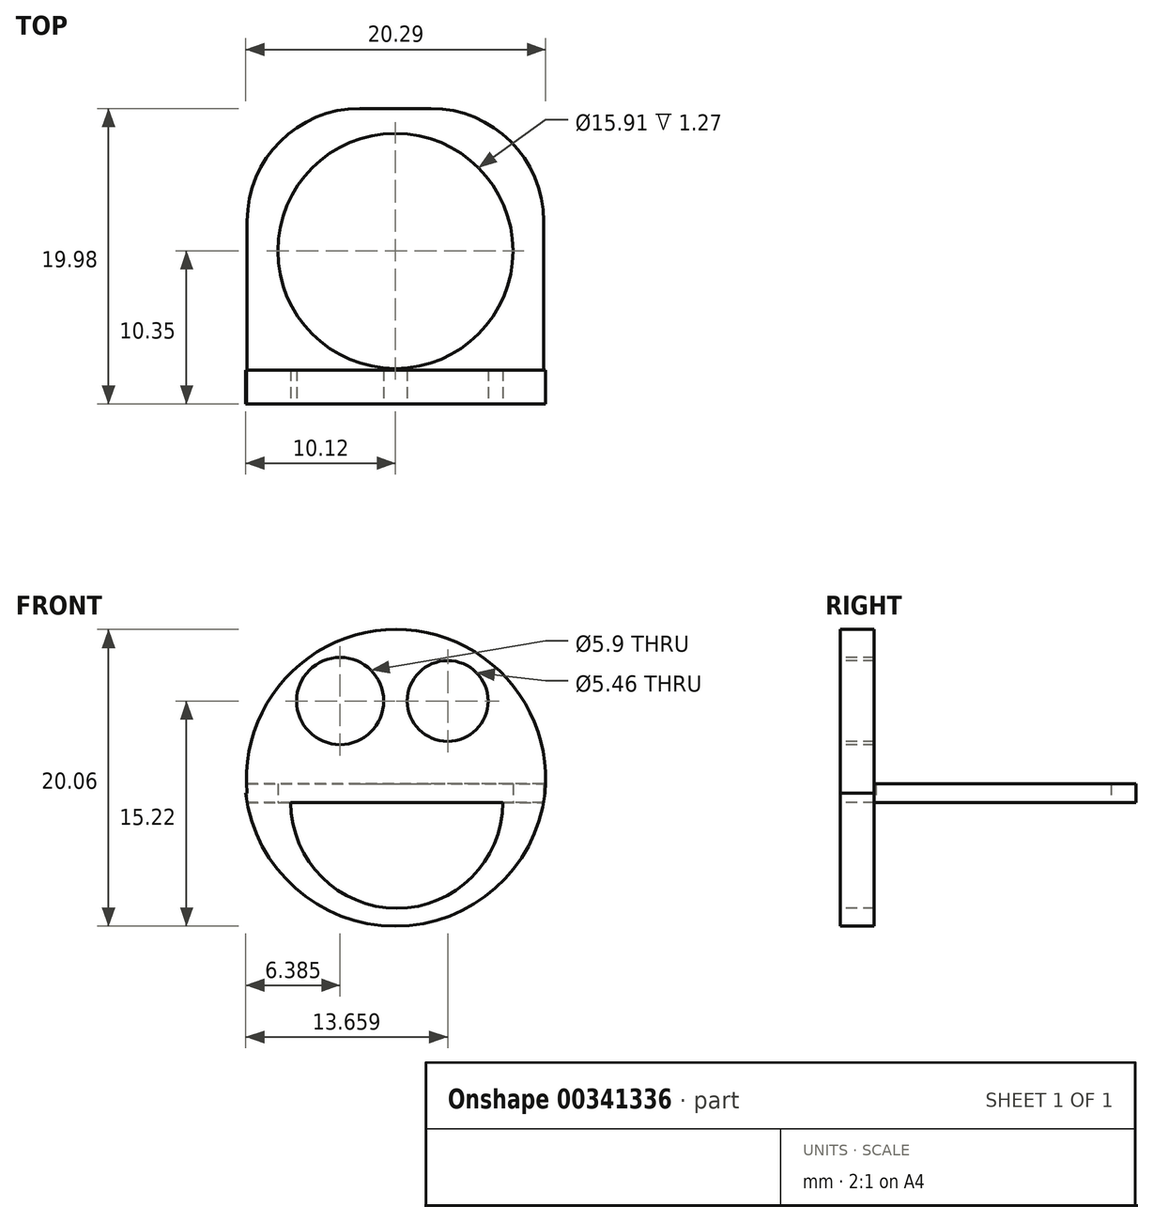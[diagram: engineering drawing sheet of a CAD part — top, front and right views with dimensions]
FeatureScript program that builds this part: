
annotation { "Feature Type Name" : "Feature", "Feature Type Description" : "" }
export const myFeature = defineFeature(function(context is Context, id is Id, definition is map)
    precondition{}
    {
        {
            var Q0;
            Q0=qCreatedBy(makeId("Top.planeOp"),FACE);
            var sketch = newSketch(context, id + "F0", { "sketchPlane" : qUnion([Q0])});
            skCircle(sketch, "E0", {"center": v(0, 0) * mm, "radius": 7.95 * mm});
            skLineSegment(sketch, "E1.bottom", {"start": v(-10.03, 9.63) * mm, "end": v(10.03, 9.63) * mm});
            skLineSegment(sketch, "E1.top", {"start": v(-10.03, -8.06) * mm, "end": v(10.03, -8.06) * mm});
            skLineSegment(sketch, "E1.left", {"start": v(-10.03, 9.63) * mm, "end": v(-10.03, -8.06) * mm});
            skLineSegment(sketch, "E1.right", {"start": v(10.03, 9.63) * mm, "end": v(10.03, -8.06) * mm});
            skSolve(sketch);
        }
        {
            var Q0;
            Q0 = qSketchRegion(id + "F0", true);
            extrude(context, id + "F1", {"entities" : qUnion([Q0]), "depth" : 1.27 * mm});
        }
        {
            var Q0;
            Q0=makeQuery(id+"F1.opExtrude","SWEPT_EDGE",EDGE,{"disambiguationData":[OSD([sQuery(id+"F0.wireOp",EDGE,"E1.bottom"),sQuery(id+"F0.wireOp",EDGE,"E1.left")])]});
            var Q1;
            Q1=makeQuery(id+"F1.opExtrude","SWEPT_EDGE",EDGE,{"disambiguationData":[OSD([sQuery(id+"F0.wireOp",EDGE,"E1.bottom"),sQuery(id+"F0.wireOp",EDGE,"E1.right")])]});
            fillet(context, id + "F2", {"entities" : qUnion([Q0, Q1]), "radius" : 7.62 * mm, "tangentPropagation" : true, "allowEdgeOverflow" : false});
        }
        {
            var Q0;
            Q0=makeQuery(id+"F1.opExtrude","SWEPT_FACE",FACE,{"disambiguationData":[OSD([sQuery(id+"F0.wireOp",EDGE,"E1.top")])]});
            var sketch = newSketch(context, id + "F3", { "sketchPlane" : qUnion([Q0])});
            skArc(sketch, "E2", {"start": v(-10.12, 0.64) * mm, "mid": v(0, -8.34) * mm, "end": v(10.12, 0.63) * mm});
            skPoint(sketch, "E2.centerSnap0", {"position": v(0, 1.27) * mm});
            skPoint(sketch, "E3.startSnap0", {"position": v(10.03, 0.64) * mm});
            skPoint(sketch, "E3.endSnap0", {"position": v(-10.03, 0.64) * mm});
            skLineSegment(sketch, "E4", {"start": v(-10.12, 0.64) * mm, "end": v(10.12, 0.64) * mm});
            skArc(sketch, "E5", {"start": v(10.12, 0.64) * mm, "mid": v(0.05, 11.72) * mm, "end": v(-10.03, 0.64) * mm});
            skSolve(sketch);
        }
        {
            var Q0;
            Q0 = qSketchRegion(id + "F3", true);
            extrude(context, id + "F4", {"entities" : qUnion([Q0]), "operationType" : NewBodyOperationType.ADD, "depth" : 2.3 * mm});
        }
        {
            var Q0;
            Q0=makeQuery(id+"F4.opExtrude","CAP_FACE",FACE,{"disambiguationData":[OSD([sQuery(id+"F3.wireOp",EDGE,"E2"),sQuery(id+"F3.wireOp",EDGE,"E4"),sQuery(id+"F3.wireOp",EDGE,"E5")])],"isStart":false});
            var sketch = newSketch(context, id + "F5", { "sketchPlane" : qUnion([Q0])});
            skCircle(sketch, "E6", {"center": v(-3.74, 6.88) * mm, "radius": 2.95 * mm});
            skCircle(sketch, "E7", {"center": v(3.54, 6.88) * mm, "radius": 2.73 * mm});
            skArc(sketch, "E8", {"start": v(-7.08, 0) * mm, "mid": v(0.1, -7.13) * mm, "end": v(7.27, 0) * mm});
            skLineSegment(sketch, "E9", {"start": v(-7.08, 0) * mm, "end": v(7.27, 0) * mm});
            skSolve(sketch);
        }
        {
            var Q0;
            Q0=makeQuery(id+"F5.imprint","IMPRINT",FACE,{"disambiguationData":[TD([[makeQuery(id+"F5.imprint","IMPRINT",EDGE,{"derivedFrom":sQuery(id+"F5.wireOp",EDGE,"E8")}),1.0]])]});
            var Q1;
            Q1=makeQuery(id+"F5.imprint","IMPRINT",FACE,{"disambiguationData":[TD([[makeQuery(id+"F5.imprint","IMPRINT",EDGE,{"derivedFrom":sQuery(id+"F5.wireOp",EDGE,"E7")}),1.0]])]});
            var Q2;
            Q2=makeQuery(id+"F5.imprint","IMPRINT",FACE,{"disambiguationData":[TD([[makeQuery(id+"F5.imprint","IMPRINT",EDGE,{"derivedFrom":sQuery(id+"F5.wireOp",EDGE,"E6")}),1.0]])]});
            extrude(context, id + "F6", {"entities" : qUnion([Q0, Q1, Q2]), "operationType" : NewBodyOperationType.REMOVE, "oppositeDirection" : true, "depth" : 25.4 * mm});
        }
    });
